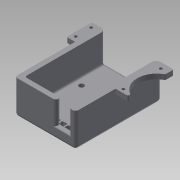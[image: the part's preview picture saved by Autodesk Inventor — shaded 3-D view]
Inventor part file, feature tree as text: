
AUTODESK INVENTOR PART (.ipt)
format: ipt  version: 2015 SP1 (Build 190203100, 203)  size: 557,568 bytes
history: native  units: mm
features: extrude x17, sketch x17, projected_geometry x11, fillet x9, reference x2
ambient origin geometry x8: Origin, YZ Plane, XZ Plane, XY Plane, X Axis, Y Axis, Z Axis, Center Point
bodies: Solid1 (feature_tree)
feature tree (56):
  extrude  "Extrusion1"  Depth=60.0mm
  extrude  "Extrusion3"  Depth=20.0mm TaperAngle=0.0deg
  extrude  "Extrusion4"  Depth=3.5mm TaperAngle=0.0deg
  extrude  "Extrusion5"  Depth=3.5mm TaperAngle=0.0deg
  extrude  "Extrusion6"  Depth=6.0mm
  extrude  "Extrusion7"  Depth=2.0mm
  extrude  "Extrusion8"  Depth=2.0mm
  fillet  "Fillet1"  Radius=2.0mm
  extrude  "Extrusion9"  Depth=3.5mm TaperAngle=0.0deg
  extrude  "Extrusion10"  Depth=3.5mm TaperAngle=0.0deg
  fillet  "Fillet2"  Radius=3.5mm
  extrude  "Extrusion11"  Depth=3.5mm TaperAngle=0.0deg
  extrude  "Extrusion12"  Depth=3.5mm TaperAngle=0.0deg
  extrude  "Extrusion13"  Depth=3.5mm
  extrude  "Extrusion14"  Depth=3.5mm
  sketch  "Sketch19"  dims[d76=3.5mm d77=3.5mm]
  fillet  "Fillet3"  Radius=3.5mm
  extrude  "Extrusion16"  Depth=3.5mm
  extrude  "Extrusion17"  Depth=12.5mm
  extrude  "Extrusion18"  Depth=3.5mm TaperAngle=0.0deg
  extrude  "Extrusion19"  Depth=3.5mm TaperAngle=0.0deg
  fillet  "Fillet5"  Radius=2.0mm
  fillet  "Fillet6"  Radius=1.0mm
  fillet  "Fillet7"  Radius=2.0mm
  fillet  "Fillet8"  Radius=1.0mm
  fillet  "Fillet9"  Radius=1.0mm
  fillet  "Fillet10"  Radius=1.0mm
  sketch  "Sketch1"  dims[d0=42.5mm d1=60.0mm]
  sketch  "Sketch4"  dims[d2=3.5mm d3=0.0mm d11=20.0mm d12=0.0mm]
  sketch  "Sketch5"  dims[d13=3.5mm d14=0.0mm d15=3.5mm d16=0.0mm]
  sketch  "Sketch6"  dims[d17=3.5mm d18=0.0mm d19=3.5mm d20=0.0mm]
  sketch  "Sketch7"  dims[d21=6.0mm d22=6.0mm]
  reference  "Reference1"
  sketch  "Sketch8"  dims[d23=3.5mm d24=2.0mm]
  reference  "Reference2"
  sketch  "Sketch11"  dims[d25=2.0mm d26=2.0mm d27=2.0mm]
  projected_geometry  "Projected Loop1"
  projected_geometry  "Projected Loop2"
  projected_geometry  "Projected Loop3"
  sketch  "Sketch12"  dims[d28=3.5mm d29=3.5mm d30=0.0mm]
  sketch  "Sketch13"  dims[d31=2.0mm d32=3.5mm d33=0.0mm d34=3.5mm d35=0.0mm]
  projected_geometry  "Projected Loop4"
  projected_geometry  "Projected Loop5"
  projected_geometry  "Projected Loop6"
  projected_geometry  "Projected Loop7"
  projected_geometry  "Projected Loop8"
  sketch  "Sketch15"  dims[d36=3.0mm d51=3.5mm d52=0.0mm]
  sketch  "Sketch16"  dims[d53=3.5mm d54=0.0mm d55=3.5mm d56=0.0mm]
  sketch  "Sketch17"  dims[d57=3.5mm d58=0.0mm d70=1.25mm]
  sketch  "Sketch18"  dims[d71=11.75mm d72=16.0mm d73=3.5mm d74=0.0mm]
  sketch  "Sketch21"  dims[d78=25.0mm d79=12.5mm]
  projected_geometry  "Projected Loop10"
  sketch  "Sketch22"  dims[d80=20.0mm d81=3.5mm d82=0.0mm]
  projected_geometry  "Projected Loop11"
  sketch  "Sketch23"  dims[d92=3.5mm d93=0.0mm d94=3.5mm d95=0.0mm d96=2.0mm d97=1.0mm d98=2.0mm d99=1.0mm d100=1.0mm d101=1.0mm]
  projected_geometry  "Projected Loop12"
